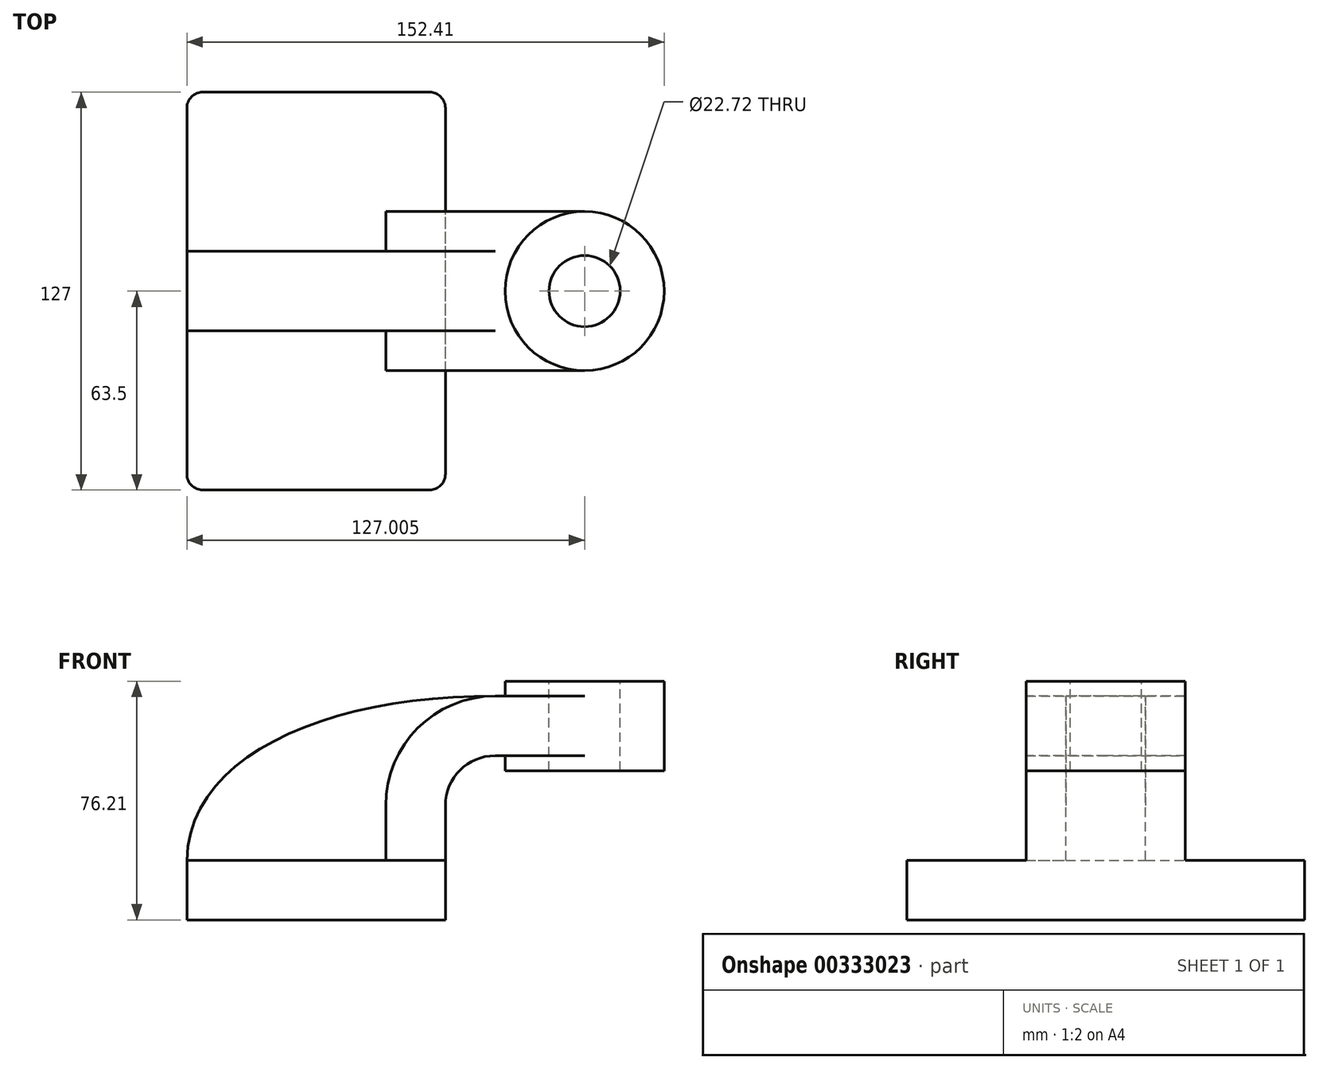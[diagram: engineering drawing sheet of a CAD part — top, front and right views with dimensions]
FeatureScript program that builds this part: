
annotation { "Feature Type Name" : "Feature", "Feature Type Description" : "" }
export const myFeature = defineFeature(function(context is Context, id is Id, definition is map)
    precondition{}
    {
        {
            var Q0;
            Q0=qCreatedBy(makeId("Front.planeOp"),FACE);
            var sketch = newSketch(context, id + "F0", { "sketchPlane" : qUnion([Q0])});
            skLineSegment(sketch, "E0.bottom", {"start": v(41.28, -9.52) * mm, "end": v(-41.27, -9.52) * mm});
            skLineSegment(sketch, "E0.top", {"start": v(41.27, 9.53) * mm, "end": v(-41.28, 9.53) * mm});
            skLineSegment(sketch, "E0.left", {"start": v(41.28, -9.52) * mm, "end": v(41.28, 9.53) * mm});
            skLineSegment(sketch, "E0.right", {"start": v(-41.27, -9.52) * mm, "end": v(-41.28, 9.53) * mm});
            skPoint(sketch, "E0.middle", {"position": v(0, 0) * mm});
            skLineSegment(sketch, "E1", {"start": v(41.27, 9.53) * mm, "end": v(41.27, 27) * mm});
            skArc(sketch, "E2", {"start": v(41.27, 27) * mm, "mid": v(45.92, 38.23) * mm, "end": v(57.15, 42.88) * mm});
            skLineSegment(sketch, "E3.bottom", {"start": v(111.13, 38.1) * mm, "end": v(60.33, 38.1) * mm});
            skLineSegment(sketch, "E3.top", {"start": v(111.13, 66.68) * mm, "end": v(60.33, 66.68) * mm});
            skLineSegment(sketch, "E3.left", {"start": v(111.13, 38.1) * mm, "end": v(111.13, 66.68) * mm});
            skLineSegment(sketch, "E3.right", {"start": v(60.33, 38.1) * mm, "end": v(60.33, 66.68) * mm});
            skPoint(sketch, "E3.middle", {"position": v(85.73, 52.39) * mm});
            skArc(sketch, "E4.1", {"start": v(22.23, 27) * mm, "mid": v(32.45, 51.7) * mm, "end": v(57.15, 61.93) * mm});
            skLineSegment(sketch, "E4.2", {"start": v(22.23, 9.53) * mm, "end": v(22.23, 27) * mm});
            skLineSegment(sketch, "E5", {"start": v(57.15, 42.88) * mm, "end": v(85.73, 42.88) * mm});
            skPoint(sketch, "E5.endSnap0", {"position": v(85.73, 38.1) * mm});
            skLineSegment(sketch, "E6", {"start": v(57.15, 61.93) * mm, "end": v(85.73, 61.93) * mm});
            skLineSegment(sketch, "E7", {"start": v(41.27, 9.53) * mm, "end": v(22.23, 9.53) * mm});
            skLineSegment(sketch, "E8", {"start": v(85.73, 38.1) * mm, "end": v(85.73, 66.68) * mm});
            skFitSpline(sketch, "E9", {"points": [v(-41.28, 9.53) * mm, v(57.15, 61.93) * mm], "startDerivative": vector(2.26, 103.07) * mm, "endDerivative": vector(155.84, -0.57) * mm});
            skSolve(sketch);
        }
        {
            var Q0;
            Q0=makeQuery(id+"F0.imprint","IMPRINT",FACE,{"disambiguationData":[TD([[makeQuery(id+"F0.imprint","IMPRINT",EDGE,{"derivedFrom":sQuery(id+"F0.wireOp",EDGE,"E0.bottom")}),-1.0]])]});
            extrude(context, id + "F1", {"entities" : qUnion([Q0]), "endBound" : BoundingType.SYMMETRIC, "depth" : 127 * mm});
        }
        {
            var Q0;
            Q0=makeQuery(id+"F0.imprint","IMPRINT",FACE,{"disambiguationData":[TD([[makeQuery(id+"F0.imprint","IMPRINT",EDGE,{"derivedFrom":sQuery(id+"F0.wireOp",EDGE,"E1")}),1.0]])]});
            var Q1;
            {var subQ0=sQuery(id+"F0.wireOp",EDGE,"E5");var subQ1=sQuery(id+"F0.wireOp",EDGE,"E3.right");var subQ2=makeQuery(id+"F0.imprint","INTERSECT",VERTEX,{"derivedFrom":[subQ1,subQ0]});Q1=makeQuery(id+"F0.imprint","IMPRINT",FACE,{"disambiguationData":[TD([[makeQuery(id+"F0.imprint","IMPRINT",EDGE,{"disambiguationData":[TD([[subQ2,-1.0]])],"derivedFrom":subQ1}),-1.0]])]});}
            extrude(context, id + "F2", {"entities" : qUnion([Q0, Q1]), "operationType" : NewBodyOperationType.ADD, "endBound" : BoundingType.SYMMETRIC, "depth" : 50.8 * mm});
        }
        {
            var Q0;
            Q0=makeQuery(id+"F0.imprint","IMPRINT",FACE,{"disambiguationData":[TD([[makeQuery(id+"F0.imprint","IMPRINT",EDGE,{"derivedFrom":sQuery(id+"F0.wireOp",EDGE,"E0.top")}),-1.0]])]});
            extrude(context, id + "F3", {"entities" : qUnion([Q0]), "operationType" : NewBodyOperationType.ADD, "endBound" : BoundingType.SYMMETRIC, "depth" : 25.4 * mm});
        }
        {
            var Q0;
            {var subQ0=sQuery(id+"F0.wireOp",EDGE,"E3.left");Q0=makeQuery(id+"F0.imprint","IMPRINT",FACE,{"disambiguationData":[TD([[makeQuery(id+"F0.imprint","IMPRINT",EDGE,{"derivedFrom":subQ0}),1.0]])]});}
            var Q1;
            Q1=sQuery(id+"F0.wireOp",EDGE,"E8");
            revolve(context, id + "F4", {"operationType" : NewBodyOperationType.ADD, "entities" : qUnion([Q0]), "axis" : qUnion([Q1]), "revolveType" : RevolveType.FULL});
        }
        {
            var Q0;
            Q0=makeQuery(id+"F1.opExtrude","CAP_EDGE",EDGE,{"disambiguationData":[OSD([sQuery(id+"F0.wireOp",EDGE,"E0.left")])],"isStart":false});
            var Q1;
            Q1=makeQuery(id+"F1.opExtrude","CAP_EDGE",EDGE,{"disambiguationData":[OSD([sQuery(id+"F0.wireOp",EDGE,"E0.right")])],"isStart":false});
            var Q2;
            Q2=makeQuery(id+"F1.opExtrude","CAP_EDGE",EDGE,{"disambiguationData":[OSD([sQuery(id+"F0.wireOp",EDGE,"E0.right")])],"isStart":true});
            var Q3;
            Q3=makeQuery(id+"F1.opExtrude","CAP_EDGE",EDGE,{"disambiguationData":[OSD([sQuery(id+"F0.wireOp",EDGE,"E0.left")])],"isStart":true});
            fillet(context, id + "F5", {"entities" : qUnion([Q0, Q1, Q2, Q3]), "radius" : 5.08 * mm, "tangentPropagation" : true, "allowEdgeOverflow" : false});
        }
        {
            var Q0;
            Q0=makeQuery(id+"F4.opRevolve","SWEPT_FACE",FACE,{"disambiguationData":[OSD([sQuery(id+"F0.wireOp",EDGE,"E3.top")])]});
            var sketch = newSketch(context, id + "F6", { "sketchPlane" : qUnion([Q0])});
            skCircle(sketch, "E10", {"center": v(85.73, 0) * mm, "radius": 11.36 * mm});
            skSolve(sketch);
        }
        {
            var Q0;
            Q0 = qSketchRegion(id + "F6", true);
            extrude(context, id + "F7", {"entities" : qUnion([Q0]), "operationType" : NewBodyOperationType.REMOVE, "oppositeDirection" : true, "depth" : 28.57 * mm});
        }
    });
